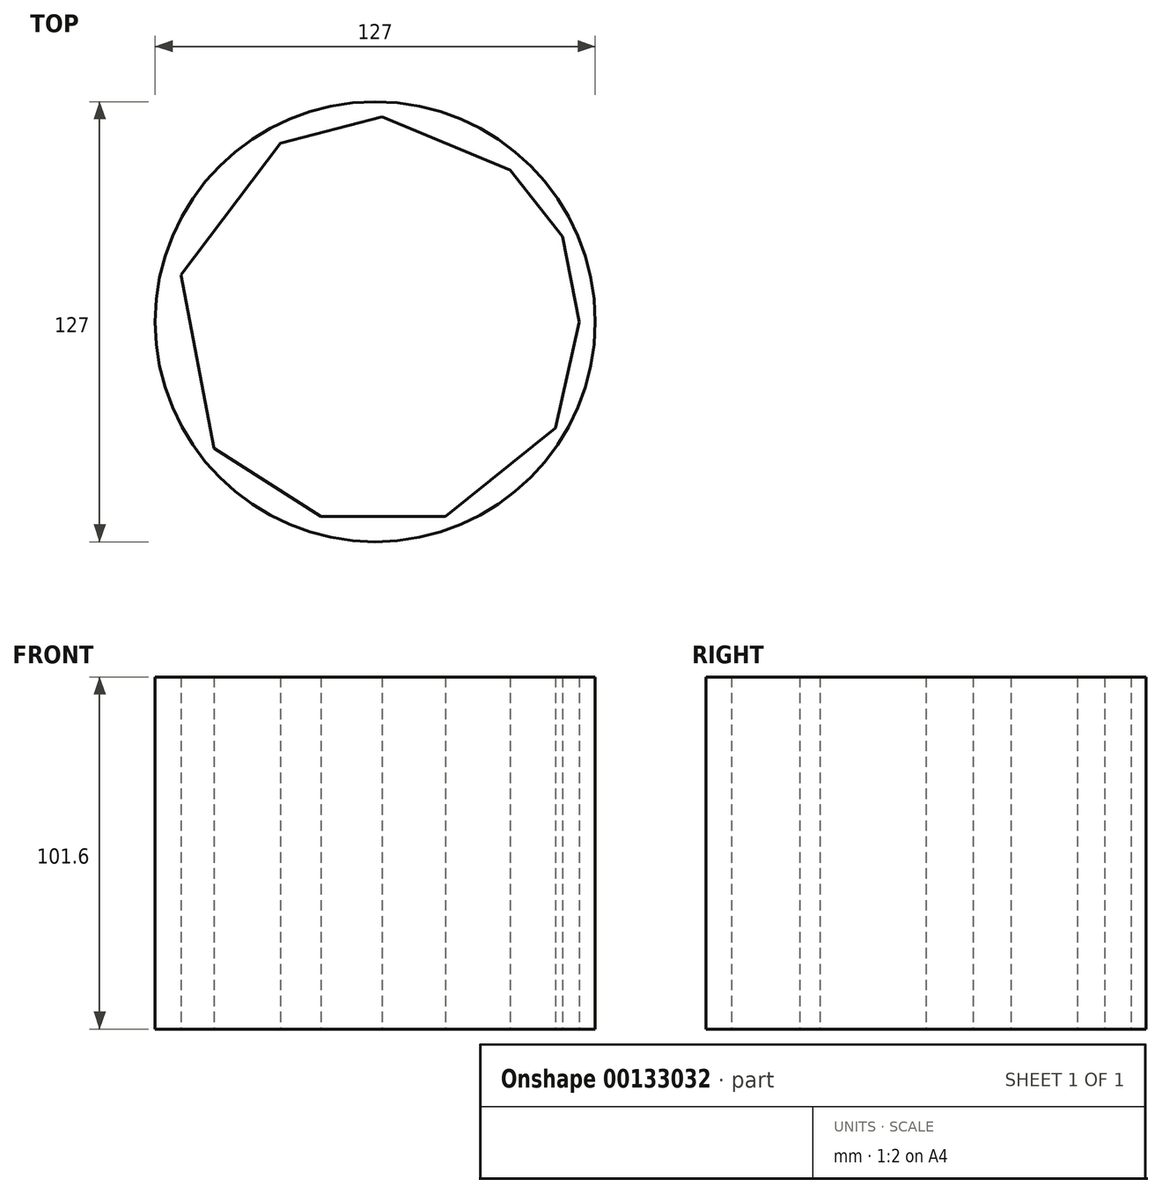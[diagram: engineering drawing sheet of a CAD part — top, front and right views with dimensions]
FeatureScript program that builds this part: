
annotation { "Feature Type Name" : "Feature", "Feature Type Description" : "" }
export const myFeature = defineFeature(function(context is Context, id is Id, definition is map)
    precondition{}
    {
        {
            var Q0;
            Q0=qCreatedBy(makeId("Top.planeOp"),FACE);
            var sketch = newSketch(context, id + "F0", { "sketchPlane" : qUnion([Q0])});
            skCircle(sketch, "E0", {"center": v(0, 0) * mm, "radius": 63.5 * mm});
            skCircle(sketch, "E1", {"center": v(2.42, 0) * mm, "radius": 50.8 * mm});
            skLineSegment(sketch, "E2", {"start": v(-46.47, -36.45) * mm, "end": v(-56.05, 13.5) * mm});
            skLineSegment(sketch, "E3", {"start": v(-56.05, 13.5) * mm, "end": v(-27.3, 51.55) * mm});
            skLineSegment(sketch, "E4", {"start": v(-27.3, 51.55) * mm, "end": v(2.03, 59.1) * mm});
            skLineSegment(sketch, "E5", {"start": v(2.03, 59.1) * mm, "end": v(38.92, 43.7) * mm});
            skLineSegment(sketch, "E6", {"start": v(38.92, 43.7) * mm, "end": v(54.02, 24.54) * mm});
            skLineSegment(sketch, "E7", {"start": v(54.02, 24.54) * mm, "end": v(58.95, 0) * mm});
            skLineSegment(sketch, "E8", {"start": v(58.95, 0) * mm, "end": v(51.98, -30.64) * mm});
            skLineSegment(sketch, "E9", {"start": v(51.98, -30.64) * mm, "end": v(20.33, -56.2) * mm});
            skLineSegment(sketch, "E10", {"start": v(20.33, -56.2) * mm, "end": v(-15.68, -56.2) * mm});
            skLineSegment(sketch, "E11", {"start": v(-15.68, -56.2) * mm, "end": v(-46.47, -36.45) * mm});
            skSolve(sketch);
        }
        {
            var Q0;
            Q0=makeQuery(id+"F0.imprint","IMPRINT",FACE,{"disambiguationData":[TD([[makeQuery(id+"F0.imprint","IMPRINT",EDGE,{"derivedFrom":sQuery(id+"F0.wireOp",EDGE,"E0")}),1.0]])]});
            extrude(context, id + "F1", {"entities" : qUnion([Q0]), "depth" : 101.6 * mm});
        }
        {
            var Q0;
            Q0 = qSketchRegion(id + "F0", true);
            extrude(context, id + "F2", {"entities" : qUnion([Q0]), "operationType" : NewBodyOperationType.ADD, "depth" : 101.6 * mm});
        }
        {
            var Q0;
            Q0 = qSketchRegion(id + "F0", true);
            extrude(context, id + "F3", {"entities" : qUnion([Q0]), "operationType" : NewBodyOperationType.ADD, "depth" : 25.4 * mm});
        }
        {
            var Q0;
            Q0 = qSketchRegion(id + "F0", true);
            extrude(context, id + "F4", {"entities" : qUnion([Q0]), "operationType" : NewBodyOperationType.ADD, "depth" : 101.6 * mm});
        }
    });
